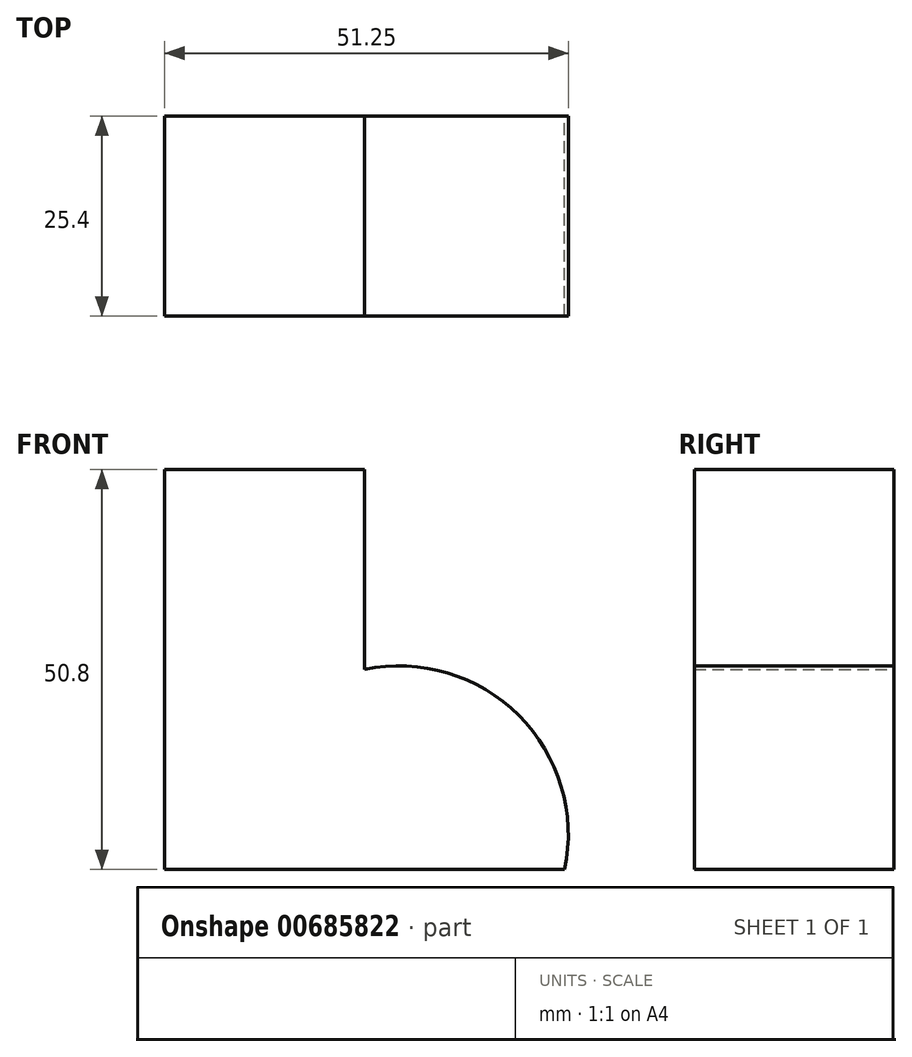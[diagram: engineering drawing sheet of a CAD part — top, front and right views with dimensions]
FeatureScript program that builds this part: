
annotation { "Feature Type Name" : "Feature", "Feature Type Description" : "" }
export const myFeature = defineFeature(function(context is Context, id is Id, definition is map)
    precondition{}
    {
        {
            var Q0;
            Q0=qCreatedBy(makeId("Front.planeOp"),FACE);
            var sketch = newSketch(context, id + "F0", { "sketchPlane" : qUnion([Q0])});
            skLineSegment(sketch, "E0", {"start": v(-57.2, 27.98) * mm, "end": v(-57.2, -22.82) * mm});
            skLineSegment(sketch, "E1", {"start": v(-57.2, -22.82) * mm, "end": v(-6.4, -22.82) * mm});
            skLineSegment(sketch, "E2", {"start": v(-57.2, 27.98) * mm, "end": v(-31.8, 27.98) * mm});
            skLineSegment(sketch, "E3", {"start": v(-31.8, 27.98) * mm, "end": v(-31.8, 2.58) * mm});
            skArc(sketch, "E4", {"start": v(-6.4, -22.82) * mm, "mid": v(-12.23, -3.26) * mm, "end": v(-31.8, 2.58) * mm});
            skSolve(sketch);
        }
        {
            var Q0;
            Q0 = qSketchRegion(id + "F0", true);
            extrude(context, id + "F1", {"entities" : qUnion([Q0]), "depth" : 25.4 * mm, "offsetDistance" : 25.4 * mm});
        }
    });
